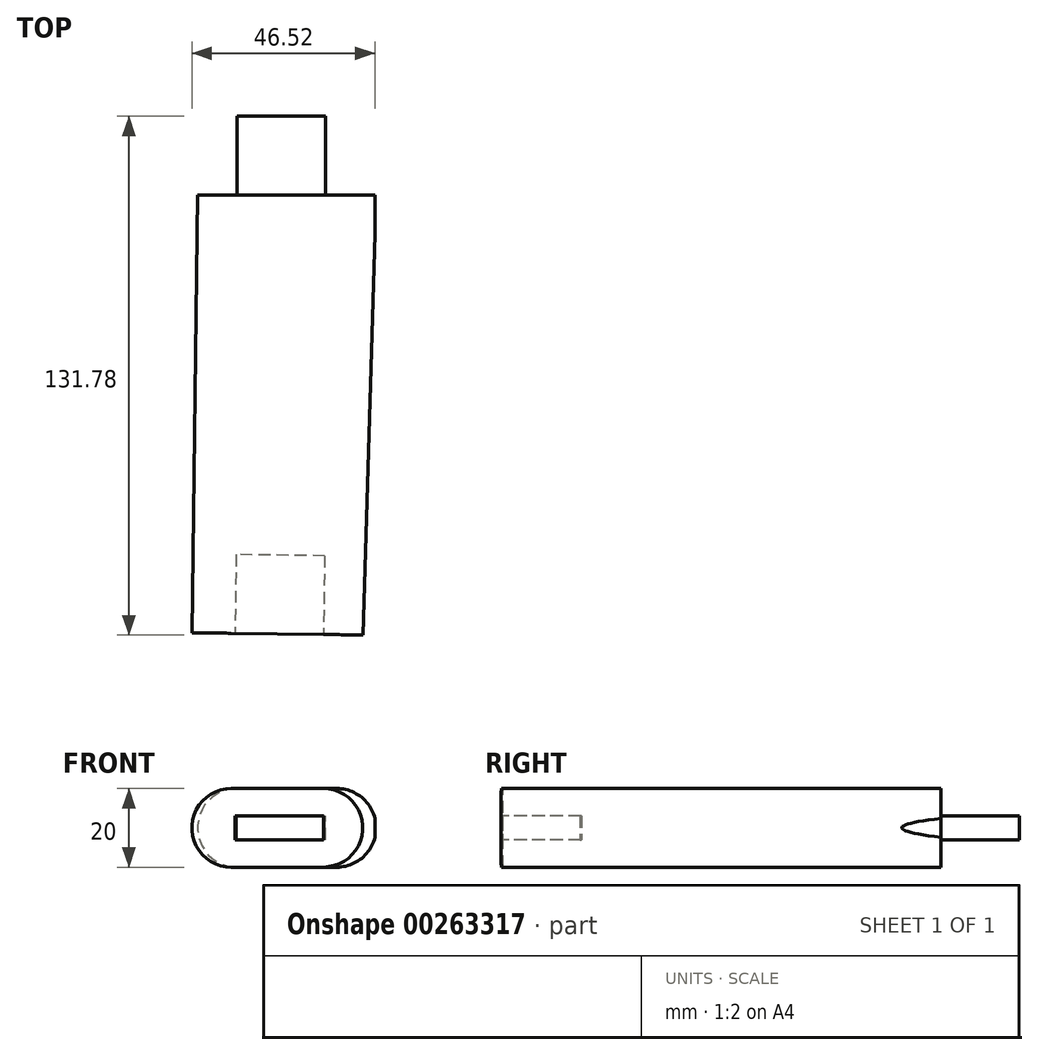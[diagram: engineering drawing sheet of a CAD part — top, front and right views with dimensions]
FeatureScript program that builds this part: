
annotation { "Feature Type Name" : "Feature", "Feature Type Description" : "" }
export const myFeature = defineFeature(function(context is Context, id is Id, definition is map)
    precondition{}
    {
        {
            var Q0;
            Q0=qCreatedBy(makeId("Top.planeOp"),FACE);
            var sketch = newSketch(context, id + "F0", { "sketchPlane" : qUnion([Q0])});
            skArc(sketch, "E0", {"start": v(-69.56, -48.3) * mm, "mid": v(-88.08, -45.25) * mm, "end": v(-106.8, -43.78) * mm});
            skArc(sketch, "E1", {"start": v(-106.8, -43.78) * mm, "mid": v(-96.39, -62.57) * mm, "end": v(-80.73, -77.27) * mm});
            skArc(sketch, "E2", {"start": v(-80.73, -77.27) * mm, "mid": v(-98.26, -84.7) * mm, "end": v(-114.23, -95.07) * mm});
            skArc(sketch, "E3", {"start": v(-114.23, -95.07) * mm, "mid": v(-98.6, -104.41) * mm, "end": v(-80.73, -107.98) * mm});
            skArc(sketch, "E4", {"start": v(-80.73, -107.98) * mm, "mid": v(-90.04, -123.58) * mm, "end": v(-94.69, -141.13) * mm});
            skArc(sketch, "E5", {"start": v(-94.69, -141.13) * mm, "mid": v(-78.8, -139.7) * mm, "end": v(-63.98, -133.8) * mm});
            skArc(sketch, "E6", {"start": v(-63.98, -133.8) * mm, "mid": v(40.14, -139.24) * mm, "end": v(30.94, -35.4) * mm});
            skArc(sketch, "E7", {"start": v(-31.41, -22.87) * mm, "mid": v(-53.17, -31.57) * mm, "end": v(-69.56, -48.3) * mm});
            skCircle(sketch, "E8", {"center": v(-12, -90) * mm, "radius": 35 * mm});
            skLineSegment(sketch, "E9", {"start": v(-12, -90) * mm, "end": v(-12, 0) * mm});
            skLineSegment(sketch, "E10", {"start": v(-12, 0) * mm, "end": v(0, 0) * mm});
            skLineSegment(sketch, "E11", {"start": v(-31.41, -22.87) * mm, "end": v(-12, 0) * mm});
            skLineSegment(sketch, "E12", {"start": v(-31.41, -22.87) * mm, "end": v(0, 0) * mm});
            skArc(sketch, "E13", {"start": v(30.94, -35.4) * mm, "mid": v(57.65, 8.29) * mm, "end": v(64.82, 58.99) * mm});
            skLineSegment(sketch, "E14", {"start": v(64.82, 42.9) * mm, "end": v(70.1, 125.75) * mm});
            skLineSegment(sketch, "E15", {"start": v(70.1, 125.75) * mm, "end": v(73.47, 146.99) * mm});
            skLineSegment(sketch, "E16", {"start": v(73.47, 146.99) * mm, "end": v(91.25, 150.97) * mm});
            skArc(sketch, "E17", {"start": v(93.55, 168.05) * mm, "mid": v(98.13, 170.3) * mm, "end": v(101.04, 174.5) * mm});
            skArc(sketch, "E18", {"start": v(101.04, 174.5) * mm, "mid": v(98.19, 178.86) * mm, "end": v(93.55, 181.22) * mm});
            skArc(sketch, "E19", {"start": v(91.25, 150.97) * mm, "mid": v(97.19, 153.5) * mm, "end": v(101.85, 157.96) * mm});
            skArc(sketch, "E20", {"start": v(101.85, 157.96) * mm, "mid": v(99.5, 164.5) * mm, "end": v(93.55, 168.05) * mm});
            skArc(sketch, "E21", {"start": v(93.55, 181.22) * mm, "mid": v(100.45, 185.24) * mm, "end": v(104.38, 192.2) * mm});
            skArc(sketch, "E22", {"start": v(16.27, 5.35) * mm, "mid": v(27.94, 20.47) * mm, "end": v(35.96, 37.8) * mm});
            skLineSegment(sketch, "E23", {"start": v(16.27, 5.35) * mm, "end": v(12.02, 0.97) * mm});
            skLineSegment(sketch, "E24", {"start": v(12.02, 54.47) * mm, "end": v(16.98, 220.58) * mm});
            skLineSegment(sketch, "E25", {"start": v(16.98, 220.58) * mm, "end": v(16.98, 230.48) * mm});
            skArc(sketch, "E26", {"start": v(20.74, 234.78) * mm, "mid": v(18.05, 233.34) * mm, "end": v(16.98, 230.48) * mm});
            skLineSegment(sketch, "E27", {"start": v(20.74, 234.78) * mm, "end": v(55.67, 234.78) * mm});
            skArc(sketch, "E28", {"start": v(55.67, 234.78) * mm, "mid": v(75.45, 242.82) * mm, "end": v(84, 262.38) * mm});
            skArc(sketch, "E29", {"start": v(84, 262.38) * mm, "mid": v(83.8, 275) * mm, "end": v(79.59, 286.9) * mm});
            skArc(sketch, "E30", {"start": v(79.59, 286.9) * mm, "mid": v(90.12, 305.47) * mm, "end": v(96.46, 325.87) * mm});
            skArc(sketch, "E31", {"start": v(96.46, 325.87) * mm, "mid": v(80.34, 314.22) * mm, "end": v(65.52, 300.95) * mm});
            skArc(sketch, "E32", {"start": v(65.52, 300.95) * mm, "mid": v(66.02, 314.82) * mm, "end": v(65.52, 328.68) * mm});
            skArc(sketch, "E33", {"start": v(41.86, 304.54) * mm, "mid": v(40.03, 315.53) * mm, "end": v(35.9, 325.87) * mm});
            skArc(sketch, "E34", {"start": v(35.9, 325.87) * mm, "mid": v(29.68, 316.4) * mm, "end": v(23.68, 306.81) * mm});
            skArc(sketch, "E35", {"start": v(23.68, 306.81) * mm, "mid": v(-21.12, 284.92) * mm, "end": v(-28, 235.53) * mm});
            skLineSegment(sketch, "E36", {"start": v(-31.41, -22.87) * mm, "end": v(-28, 235.53) * mm});
            skLineSegment(sketch, "E37", {"start": v(0, 0) * mm, "end": v(0, 302.13) * mm});
            skLineSegment(sketch, "E38", {"start": v(12.02, 0.97) * mm, "end": v(-31.41, -22.87) * mm});
            skLineSegment(sketch, "E39", {"start": v(0, 0) * mm, "end": v(12.02, 0.97) * mm});
            skLineSegment(sketch, "E40", {"start": v(12.02, 0.97) * mm, "end": v(30.94, -35.4) * mm});
            skLineSegment(sketch, "E41", {"start": v(64.82, 58.99) * mm, "end": v(46.6, 104.17) * mm});
            skLineSegment(sketch, "E42", {"start": v(12.02, 0.97) * mm, "end": v(12.02, 54.47) * mm});
            skLineSegment(sketch, "E43", {"start": v(-29.54, 119.27) * mm, "end": v(13.94, 118.7) * mm});
            skLineSegment(sketch, "E44", {"start": v(35.96, 37.8) * mm, "end": v(38.97, 138.47) * mm});
            skArc(sketch, "E45", {"start": v(104.38, 192.2) * mm, "mid": v(74.78, 206.52) * mm, "end": v(46.71, 189.39) * mm});
            skArc(sketch, "E46", {"start": v(46.71, 189.39) * mm, "mid": v(41.3, 164.16) * mm, "end": v(38.97, 138.47) * mm});
            skLineSegment(sketch, "E47", {"start": v(104.38, 192.2) * mm, "end": v(93.55, 181.22) * mm});
            skLineSegment(sketch, "E48", {"start": v(93.55, 168.05) * mm, "end": v(101.85, 157.96) * mm});
            skLineSegment(sketch, "E49", {"start": v(93.55, 181.22) * mm, "end": v(101.04, 174.5) * mm});
            skLineSegment(sketch, "E50", {"start": v(93.55, 168.05) * mm, "end": v(101.04, 174.5) * mm});
            skLineSegment(sketch, "E51", {"start": v(41.86, 304.54) * mm, "end": v(65.52, 328.68) * mm});
            skLineSegment(sketch, "E52", {"start": v(16.98, 230.48) * mm, "end": v(-28.07, 230.48) * mm});
            skLineSegment(sketch, "E53", {"start": v(12.02, 0.97) * mm, "end": v(-31.1, 0.49) * mm});
            skPoint(sketch, "E53.endSnap0", {"position": v(6.01, 0.49) * mm});
            skLineSegment(sketch, "E54", {"start": v(12.02, 0.97) * mm, "end": v(43.15, -20.17) * mm});
            skSolve(sketch);
        }
        {
            var Q0;
            {var subQ0=sQuery(id+"F0.wireOp",EDGE,"E38");var subQ1=sQuery(id+"F0.wireOp",EDGE,"E9");var subQ2=makeQuery(id+"F0.imprint","INTERSECT",VERTEX,{"derivedFrom":[subQ1,subQ0]});Q0=makeQuery(id+"F0.imprint","IMPRINT",FACE,{"disambiguationData":[TD([[makeQuery(id+"F0.imprint","IMPRINT",EDGE,{"disambiguationData":[TD([[subQ2,-1.0]])],"derivedFrom":subQ1}),1.0]])]});}
            var Q1;
            {var subQ0=sQuery(id+"F0.wireOp",EDGE,"E11");Q1=makeQuery(id+"F0.imprint","IMPRINT",FACE,{"disambiguationData":[TD([[makeQuery(id+"F0.imprint","IMPRINT",EDGE,{"derivedFrom":subQ0}),-1.0]])]});}
            var Q2;
            {var subQ0=sQuery(id+"F0.wireOp",EDGE,"E39");Q2=makeQuery(id+"F0.imprint","IMPRINT",FACE,{"disambiguationData":[TD([[makeQuery(id+"F0.imprint","IMPRINT",EDGE,{"derivedFrom":subQ0}),1.0]])]});}
            var Q3;
            Q3=makeQuery(id+"F0.imprint","IMPRINT",FACE,{"disambiguationData":[TD([[makeQuery(id+"F0.imprint","IMPRINT",EDGE,{"derivedFrom":sQuery(id+"F0.wireOp",EDGE,"E0")}),1.0]])]});
            var Q4;
            {var subQ5=sQuery(id+"F0.wireOp",EDGE,"E39");Q4=makeQuery(id+"F0.imprint","IMPRINT",FACE,{"disambiguationData":[TD([[makeQuery(id+"F0.imprint","IMPRINT",EDGE,{"derivedFrom":subQ5}),-1.0]])]});}
            var Q5;
            {var subQ2=sQuery(id+"F0.wireOp",EDGE,"E10");Q5=makeQuery(id+"F0.imprint","IMPRINT",FACE,{"disambiguationData":[TD([[makeQuery(id+"F0.imprint","IMPRINT",EDGE,{"derivedFrom":subQ2}),1.0]])]});}
            var Q6;
            {var subQ0=sQuery(id+"F0.wireOp",EDGE,"E10");Q6=makeQuery(id+"F0.imprint","IMPRINT",FACE,{"disambiguationData":[TD([[makeQuery(id+"F0.imprint","IMPRINT",EDGE,{"derivedFrom":subQ0}),-1.0]])]});}
            var Q7;
            {var subQ0=sQuery(id+"F0.wireOp",EDGE,"E40");Q7=makeQuery(id+"F0.imprint","IMPRINT",FACE,{"disambiguationData":[TD([[makeQuery(id+"F0.imprint","IMPRINT",EDGE,{"derivedFrom":subQ0}),1.0]])]});}
            extrude(context, id + "F1", {"entities" : qUnion([Q0, Q1, Q2, Q3, Q4, Q5, Q6, Q7]), "depth" : 20 * mm});
        }
        {
            var Q0;
            {var subQ1=sQuery(id+"F0.wireOp",EDGE,"E14");Q0=makeQuery(id+"F0.imprint","IMPRINT",FACE,{"disambiguationData":[TD([[makeQuery(id+"F0.imprint","IMPRINT",EDGE,{"derivedFrom":subQ1}),1.0]])]});}
            extrude(context, id + "F2", {"entities" : qUnion([Q0]), "depth" : 20 * mm});
        }
        {
            var Q0;
            {var subQ0=sQuery(id+"F0.wireOp",EDGE,"E43");var subQ1=sQuery(id+"F0.wireOp",EDGE,"E36");var subQ2=makeQuery(id+"F0.imprint","INTERSECT",VERTEX,{"derivedFrom":[subQ1,subQ0]});Q0=makeQuery(id+"F0.imprint","IMPRINT",FACE,{"disambiguationData":[TD([[makeQuery(id+"F0.imprint","IMPRINT",EDGE,{"disambiguationData":[TD([[subQ2,1.0]])],"derivedFrom":subQ1}),-1.0]])]});}
            var Q1;
            {var subQ5=sQuery(id+"F0.wireOp",EDGE,"E42");Q1=makeQuery(id+"F0.imprint","IMPRINT",FACE,{"disambiguationData":[TD([[makeQuery(id+"F0.imprint","IMPRINT",EDGE,{"derivedFrom":subQ5}),1.0]])]});}
            extrude(context, id + "F3", {"entities" : qUnion([Q0, Q1]), "depth" : 20 * mm});
        }
        {
            var Q0;
            {var subQ0=sQuery(id+"F0.wireOp",EDGE,"E36");var subQ1=sQuery(id+"F0.wireOp",EDGE,"E35");var subQ2=makeQuery(id+"F0.imprint","INTERSECT",VERTEX,{"derivedFrom":[subQ1,subQ0]});Q0=makeQuery(id+"F0.imprint","IMPRINT",FACE,{"disambiguationData":[TD([[makeQuery(id+"F0.imprint","IMPRINT",EDGE,{"disambiguationData":[TD([[subQ2,1.0]])],"derivedFrom":subQ1}),1.0]])]});}
            var Q1;
            {var subQ4=sQuery(id+"F0.wireOp",EDGE,"E26");Q1=makeQuery(id+"F0.imprint","IMPRINT",FACE,{"disambiguationData":[TD([[makeQuery(id+"F0.imprint","IMPRINT",EDGE,{"derivedFrom":subQ4}),-1.0]])]});}
            extrude(context, id + "F4", {"entities" : qUnion([Q0, Q1]), "depth" : 20 * mm});
        }
        {
            var Q0;
            {var subQ0=sQuery(id+"F0.wireOp",EDGE,"E43");var subQ1=sQuery(id+"F0.wireOp",EDGE,"E36");var subQ2=makeQuery(id+"F0.imprint","INTERSECT",VERTEX,{"derivedFrom":[subQ1,subQ0]});Q0=makeQuery(id+"F0.imprint","IMPRINT",FACE,{"disambiguationData":[TD([[makeQuery(id+"F0.imprint","IMPRINT",EDGE,{"disambiguationData":[TD([[subQ2,-1.0]])],"derivedFrom":subQ1}),-1.0]])]});}
            var Q1;
            {var subQ7=sQuery(id+"F0.wireOp",EDGE,"E25");Q1=makeQuery(id+"F0.imprint","IMPRINT",FACE,{"disambiguationData":[TD([[makeQuery(id+"F0.imprint","IMPRINT",EDGE,{"derivedFrom":subQ7}),1.0]])]});}
            extrude(context, id + "F5", {"entities" : qUnion([Q0, Q1]), "depth" : 20 * mm});
        }
        {
            var Q0;
            Q0=makeQuery(id+"F1.opExtrude","CAP_EDGE",EDGE,{"disambiguationData":[OSD([sQuery(id+"F0.wireOp",EDGE,"E36")])],"isStart":false});
            var Q1;
            Q1=makeQuery(id+"F1.opExtrude","CAP_EDGE",EDGE,{"disambiguationData":[OSD([sQuery(id+"F0.wireOp",EDGE,"E24")])],"isStart":false});
            var Q2;
            Q2=makeQuery(id+"F1.opExtrude","CAP_EDGE",EDGE,{"disambiguationData":[OSD([sQuery(id+"F0.wireOp",EDGE,"E42")])],"isStart":false});
            var Q3;
            Q3=makeQuery(id+"F1.opExtrude","CAP_EDGE",EDGE,{"disambiguationData":[OSD([sQuery(id+"F0.wireOp",EDGE,"E25")])],"isStart":false});
            var Q4;
            Q4=makeQuery(id+"F1.opExtrude","CAP_EDGE",EDGE,{"disambiguationData":[OSD([sQuery(id+"F0.wireOp",EDGE,"E35")])],"isStart":false});
            var Q5;
            Q5=makeQuery(id+"F1.opExtrude","CAP_EDGE",EDGE,{"disambiguationData":[OSD([sQuery(id+"F0.wireOp",EDGE,"E26")])],"isStart":false});
            var Q6;
            Q6=makeQuery(id+"F1.opExtrude","CAP_EDGE",EDGE,{"disambiguationData":[OSD([sQuery(id+"F0.wireOp",EDGE,"E42")])],"isStart":true});
            var Q7;
            Q7=makeQuery(id+"F1.opExtrude","CAP_EDGE",EDGE,{"disambiguationData":[OSD([sQuery(id+"F0.wireOp",EDGE,"E25")])],"isStart":true});
            var Q8;
            Q8=makeQuery(id+"F1.opExtrude","CAP_EDGE",EDGE,{"disambiguationData":[OSD([sQuery(id+"F0.wireOp",EDGE,"E36")])],"isStart":true});
            var Q9;
            Q9=makeQuery(id+"F1.opExtrude","CAP_EDGE",EDGE,{"disambiguationData":[OSD([sQuery(id+"F0.wireOp",EDGE,"E35")])],"isStart":true});
            var Q10;
            Q10=makeQuery(id+"F1.opExtrude","CAP_EDGE",EDGE,{"disambiguationData":[OSD([sQuery(id+"F0.wireOp",EDGE,"E26")])],"isStart":true});
            var Q11;
            Q11=makeQuery(id+"F1.opExtrude","CAP_EDGE",EDGE,{"disambiguationData":[OSD([sQuery(id+"F0.wireOp",EDGE,"E22")])],"isStart":false});
            var Q12;
            Q12=makeQuery(id+"F1.opExtrude","CAP_EDGE",EDGE,{"disambiguationData":[OSD([sQuery(id+"F0.wireOp",EDGE,"E23")])],"isStart":false});
            var Q13;
            Q13=makeQuery(id+"F1.opExtrude","CAP_EDGE",EDGE,{"disambiguationData":[OSD([sQuery(id+"F0.wireOp",EDGE,"E44")])],"isStart":false});
            var Q14;
            Q14=makeQuery(id+"F1.opExtrude","CAP_EDGE",EDGE,{"disambiguationData":[OSD([sQuery(id+"F0.wireOp",EDGE,"E45")])],"isStart":false});
            var Q15;
            Q15=makeQuery(id+"F1.opExtrude","CAP_EDGE",EDGE,{"disambiguationData":[OSD([sQuery(id+"F0.wireOp",EDGE,"E22")])],"isStart":true});
            var Q16;
            Q16=makeQuery(id+"F1.opExtrude","CAP_EDGE",EDGE,{"disambiguationData":[OSD([sQuery(id+"F0.wireOp",EDGE,"E44")])],"isStart":true});
            var Q17;
            Q17=makeQuery(id+"F1.opExtrude","CAP_EDGE",EDGE,{"disambiguationData":[OSD([sQuery(id+"F0.wireOp",EDGE,"E45")])],"isStart":true});
            var Q18;
            Q18=makeQuery(id+"F1.opExtrude","CAP_EDGE",EDGE,{"disambiguationData":[OSD([sQuery(id+"F0.wireOp",EDGE,"E13")])],"isStart":false});
            var Q19;
            Q19=makeQuery(id+"F1.opExtrude","CAP_EDGE",EDGE,{"disambiguationData":[OSD([sQuery(id+"F0.wireOp",EDGE,"E14")])],"isStart":false});
            var Q20;
            Q20=makeQuery(id+"F1.opExtrude","CAP_EDGE",EDGE,{"disambiguationData":[OSD([sQuery(id+"F0.wireOp",EDGE,"E15")])],"isStart":false});
            var Q21;
            Q21=makeQuery(id+"F1.opExtrude","CAP_EDGE",EDGE,{"disambiguationData":[OSD([sQuery(id+"F0.wireOp",EDGE,"E16")])],"isStart":false});
            var Q22;
            Q22=makeQuery(id+"F1.opExtrude","CAP_EDGE",EDGE,{"disambiguationData":[OSD([sQuery(id+"F0.wireOp",EDGE,"E16")])],"isStart":true});
            var Q23;
            Q23=makeQuery(id+"F1.opExtrude","CAP_EDGE",EDGE,{"disambiguationData":[OSD([sQuery(id+"F0.wireOp",EDGE,"E15")])],"isStart":true});
            var Q24;
            Q24=makeQuery(id+"F1.opExtrude","CAP_EDGE",EDGE,{"disambiguationData":[OSD([sQuery(id+"F0.wireOp",EDGE,"E14")])],"isStart":true});
            var Q25;
            Q25=makeQuery(id+"F1.opExtrude","CAP_EDGE",EDGE,{"disambiguationData":[OSD([sQuery(id+"F0.wireOp",EDGE,"E13")])],"isStart":true});
            var Q26;
            Q26=makeQuery(id+"F1.opExtrude","CAP_EDGE",EDGE,{"disambiguationData":[OSD([sQuery(id+"F0.wireOp",EDGE,"E6")])],"isStart":false});
            var Q27;
            Q27=makeQuery(id+"F1.opExtrude","CAP_EDGE",EDGE,{"disambiguationData":[OSD([sQuery(id+"F0.wireOp",EDGE,"E8")])],"isStart":false});
            var Q28;
            Q28=makeQuery(id+"F1.opExtrude","CAP_EDGE",EDGE,{"disambiguationData":[OSD([sQuery(id+"F0.wireOp",EDGE,"E7")])],"isStart":false});
            var Q29;
            Q29=makeQuery(id+"F1.opExtrude","CAP_EDGE",EDGE,{"disambiguationData":[OSD([sQuery(id+"F0.wireOp",EDGE,"E8")])],"isStart":true});
            var Q30;
            Q30=makeQuery(id+"F1.opExtrude","CAP_EDGE",EDGE,{"disambiguationData":[OSD([sQuery(id+"F0.wireOp",EDGE,"E7")])],"isStart":true});
            var Q31;
            Q31=makeQuery(id+"F1.opExtrude","CAP_EDGE",EDGE,{"disambiguationData":[OSD([sQuery(id+"F0.wireOp",EDGE,"E6")])],"isStart":true});
            fillet(context, id + "F6", {"entities" : qUnion([Q0, Q1, Q2, Q3, Q4, Q5, Q6, Q7, Q8, Q9, Q10, Q11, Q12, Q13, Q14, Q15, Q16, Q17, Q18, Q19, Q20, Q21, Q22, Q23, Q24, Q25, Q26, Q27, Q28, Q29, Q30, Q31]), "radius" : 10 * mm, "tangentPropagation" : true, "allowEdgeOverflow" : false});
        }
        {
            var Q0;
            Q0=makeQuery(id+"F1.opExtrude","CAP_EDGE",EDGE,{"disambiguationData":[OSD([sQuery(id+"F0.wireOp",EDGE,"E0")])],"isStart":false});
            var Q1;
            Q1=makeQuery(id+"F1.opExtrude","CAP_EDGE",EDGE,{"disambiguationData":[OSD([sQuery(id+"F0.wireOp",EDGE,"E1")])],"isStart":false});
            var Q2;
            Q2=makeQuery(id+"F1.opExtrude","CAP_EDGE",EDGE,{"disambiguationData":[OSD([sQuery(id+"F0.wireOp",EDGE,"E5")])],"isStart":false});
            var Q3;
            Q3=makeQuery(id+"F1.opExtrude","CAP_EDGE",EDGE,{"disambiguationData":[OSD([sQuery(id+"F0.wireOp",EDGE,"E4")])],"isStart":false});
            var Q4;
            Q4=makeQuery(id+"F1.opExtrude","CAP_EDGE",EDGE,{"disambiguationData":[OSD([sQuery(id+"F0.wireOp",EDGE,"E0")])],"isStart":true});
            var Q5;
            Q5=makeQuery(id+"F1.opExtrude","CAP_EDGE",EDGE,{"disambiguationData":[OSD([sQuery(id+"F0.wireOp",EDGE,"E1")])],"isStart":true});
            var Q6;
            Q6=makeQuery(id+"F1.opExtrude","CAP_EDGE",EDGE,{"disambiguationData":[OSD([sQuery(id+"F0.wireOp",EDGE,"E4")])],"isStart":true});
            var Q7;
            Q7=makeQuery(id+"F1.opExtrude","CAP_EDGE",EDGE,{"disambiguationData":[OSD([sQuery(id+"F0.wireOp",EDGE,"E5")])],"isStart":true});
            fillet(context, id + "F7", {"entities" : qUnion([Q0, Q1, Q2, Q3, Q4, Q5, Q6, Q7]), "radius" : 9.5 * mm, "tangentPropagation" : true, "rho" : 0.5, "crossSection" : FilletCrossSection.CONIC, "allowEdgeOverflow" : false});
        }
        {
            var Q0;
            Q0=makeQuery(id+"F1.opExtrude","CAP_EDGE",EDGE,{"disambiguationData":[OSD([sQuery(id+"F0.wireOp",EDGE,"E3")])],"isStart":true});
            var Q1;
            Q1=makeQuery(id+"F1.opExtrude","CAP_EDGE",EDGE,{"disambiguationData":[OSD([sQuery(id+"F0.wireOp",EDGE,"E2")])],"isStart":true});
            var Q2;
            Q2=makeQuery(id+"F1.opExtrude","CAP_EDGE",EDGE,{"disambiguationData":[OSD([sQuery(id+"F0.wireOp",EDGE,"E2")])],"isStart":false});
            var Q3;
            Q3=makeQuery(id+"F1.opExtrude","CAP_EDGE",EDGE,{"disambiguationData":[OSD([sQuery(id+"F0.wireOp",EDGE,"E3")])],"isStart":false});
            fillet(context, id + "F8", {"entities" : qUnion([Q0, Q1, Q2, Q3]), "radius" : 3 * mm, "tangentPropagation" : true, "allowEdgeOverflow" : false});
        }
        {
            var Q0;
            Q0=makeQuery(id+"F2.opExtrude","CAP_EDGE",EDGE,{"disambiguationData":[OSD([sQuery(id+"F0.wireOp",EDGE,"E14")])],"isStart":false});
            var Q1;
            Q1=makeQuery(id+"F2.opExtrude","CAP_EDGE",EDGE,{"disambiguationData":[OSD([sQuery(id+"F0.wireOp",EDGE,"E15")])],"isStart":false});
            var Q2;
            Q2=makeQuery(id+"F2.opExtrude","CAP_EDGE",EDGE,{"disambiguationData":[OSD([sQuery(id+"F0.wireOp",EDGE,"E14")])],"isStart":true});
            var Q3;
            Q3=makeQuery(id+"F2.opExtrude","CAP_EDGE",EDGE,{"disambiguationData":[OSD([sQuery(id+"F0.wireOp",EDGE,"E15")])],"isStart":true});
            var Q4;
            Q4=makeQuery(id+"F2.opExtrude","CAP_EDGE",EDGE,{"disambiguationData":[OSD([sQuery(id+"F0.wireOp",EDGE,"E16")])],"isStart":true});
            var Q5;
            Q5=makeQuery(id+"F2.opExtrude","CAP_EDGE",EDGE,{"disambiguationData":[OSD([sQuery(id+"F0.wireOp",EDGE,"E16")])],"isStart":false});
            var Q6;
            Q6=makeQuery(id+"F2.opExtrude","CAP_EDGE",EDGE,{"disambiguationData":[OSD([sQuery(id+"F0.wireOp",EDGE,"E45")])],"isStart":true});
            var Q7;
            Q7=makeQuery(id+"F2.opExtrude","CAP_EDGE",EDGE,{"disambiguationData":[OSD([sQuery(id+"F0.wireOp",EDGE,"E45")])],"isStart":false});
            var Q8;
            Q8=makeQuery(id+"F2.opExtrude","CAP_EDGE",EDGE,{"disambiguationData":[OSD([sQuery(id+"F0.wireOp",EDGE,"E46")])],"isStart":false});
            var Q9;
            Q9=makeQuery(id+"F2.opExtrude","CAP_EDGE",EDGE,{"disambiguationData":[OSD([sQuery(id+"F0.wireOp",EDGE,"E44")])],"isStart":false});
            var Q10;
            Q10=makeQuery(id+"F2.opExtrude","CAP_EDGE",EDGE,{"disambiguationData":[OSD([sQuery(id+"F0.wireOp",EDGE,"E22")])],"isStart":false});
            var Q11;
            Q11=makeQuery(id+"F2.opExtrude","CAP_EDGE",EDGE,{"disambiguationData":[OSD([sQuery(id+"F0.wireOp",EDGE,"E23")])],"isStart":false});
            var Q12;
            Q12=makeQuery(id+"F2.opExtrude","CAP_EDGE",EDGE,{"disambiguationData":[OSD([sQuery(id+"F0.wireOp",EDGE,"E46")])],"isStart":true});
            var Q13;
            Q13=makeQuery(id+"F2.opExtrude","CAP_EDGE",EDGE,{"disambiguationData":[OSD([sQuery(id+"F0.wireOp",EDGE,"E23")])],"isStart":true});
            var Q14;
            Q14=makeQuery(id+"F2.opExtrude","CAP_EDGE",EDGE,{"disambiguationData":[OSD([sQuery(id+"F0.wireOp",EDGE,"E22")])],"isStart":true});
            var Q15;
            Q15=makeQuery(id+"F2.opExtrude","CAP_EDGE",EDGE,{"disambiguationData":[OSD([sQuery(id+"F0.wireOp",EDGE,"E44")])],"isStart":true});
            var Q16;
            Q16=makeQuery(id+"F3.opExtrude","CAP_EDGE",EDGE,{"disambiguationData":[OSD([sQuery(id+"F0.wireOp",EDGE,"E24")])],"isStart":false});
            var Q17;
            Q17=makeQuery(id+"F3.opExtrude","CAP_EDGE",EDGE,{"disambiguationData":[OSD([sQuery(id+"F0.wireOp",EDGE,"E42")])],"isStart":false});
            var Q18;
            Q18=makeQuery(id+"F3.opExtrude","CAP_EDGE",EDGE,{"disambiguationData":[OSD([sQuery(id+"F0.wireOp",EDGE,"E42")])],"isStart":true});
            var Q19;
            Q19=makeQuery(id+"F3.opExtrude","CAP_EDGE",EDGE,{"disambiguationData":[OSD([sQuery(id+"F0.wireOp",EDGE,"E24")])],"isStart":true});
            var Q20;
            Q20=makeQuery(id+"F3.opExtrude","CAP_EDGE",EDGE,{"disambiguationData":[OSD([sQuery(id+"F0.wireOp",EDGE,"E25")])],"isStart":true});
            var Q21;
            Q21=makeQuery(id+"F3.opExtrude","CAP_EDGE",EDGE,{"disambiguationData":[OSD([sQuery(id+"F0.wireOp",EDGE,"E36")])],"isStart":false});
            var Q22;
            Q22=makeQuery(id+"F3.opExtrude","CAP_EDGE",EDGE,{"disambiguationData":[OSD([sQuery(id+"F0.wireOp",EDGE,"E36")])],"isStart":true});
            var Q23;
            Q23=makeQuery(id+"F4.opExtrude","CAP_EDGE",EDGE,{"disambiguationData":[OSD([sQuery(id+"F0.wireOp",EDGE,"E36")])],"isStart":true});
            var Q24;
            Q24=makeQuery(id+"F4.opExtrude","CAP_EDGE",EDGE,{"disambiguationData":[OSD([sQuery(id+"F0.wireOp",EDGE,"E36")])],"isStart":false});
            var Q25;
            Q25=makeQuery(id+"F4.opExtrude","CAP_EDGE",EDGE,{"disambiguationData":[OSD([sQuery(id+"F0.wireOp",EDGE,"E35")])],"isStart":true});
            var Q26;
            Q26=makeQuery(id+"F4.opExtrude","CAP_EDGE",EDGE,{"disambiguationData":[OSD([sQuery(id+"F0.wireOp",EDGE,"E35")])],"isStart":false});
            var Q27;
            Q27=makeQuery(id+"F4.opExtrude","CAP_EDGE",EDGE,{"disambiguationData":[OSD([sQuery(id+"F0.wireOp",EDGE,"E27")])],"isStart":false});
            var Q28;
            Q28=makeQuery(id+"F4.opExtrude","CAP_EDGE",EDGE,{"disambiguationData":[OSD([sQuery(id+"F0.wireOp",EDGE,"E28")])],"isStart":false});
            var Q29;
            Q29=makeQuery(id+"F4.opExtrude","CAP_EDGE",EDGE,{"disambiguationData":[OSD([sQuery(id+"F0.wireOp",EDGE,"E29")])],"isStart":false});
            var Q30;
            Q30=makeQuery(id+"F4.opExtrude","CAP_EDGE",EDGE,{"disambiguationData":[OSD([sQuery(id+"F0.wireOp",EDGE,"E27")])],"isStart":true});
            var Q31;
            Q31=makeQuery(id+"F4.opExtrude","CAP_EDGE",EDGE,{"disambiguationData":[OSD([sQuery(id+"F0.wireOp",EDGE,"E28")])],"isStart":true});
            var Q32;
            Q32=makeQuery(id+"F4.opExtrude","CAP_EDGE",EDGE,{"disambiguationData":[OSD([sQuery(id+"F0.wireOp",EDGE,"E29")])],"isStart":true});
            var Q33;
            Q33=makeQuery(id+"F4.opExtrude","CAP_EDGE",EDGE,{"disambiguationData":[OSD([sQuery(id+"F0.wireOp",EDGE,"E26")])],"isStart":false});
            var Q34;
            Q34=makeQuery(id+"F4.opExtrude","CAP_EDGE",EDGE,{"disambiguationData":[OSD([sQuery(id+"F0.wireOp",EDGE,"E26")])],"isStart":true});
            var Q35;
            Q35=makeQuery(id+"F4.opExtrude","CAP_EDGE",EDGE,{"disambiguationData":[OSD([sQuery(id+"F0.wireOp",EDGE,"E30")])],"isStart":false});
            var Q36;
            Q36=makeQuery(id+"F4.opExtrude","CAP_EDGE",EDGE,{"disambiguationData":[OSD([sQuery(id+"F0.wireOp",EDGE,"E31")])],"isStart":false});
            var Q37;
            Q37=makeQuery(id+"F4.opExtrude","CAP_EDGE",EDGE,{"disambiguationData":[OSD([sQuery(id+"F0.wireOp",EDGE,"E30")])],"isStart":true});
            var Q38;
            Q38=makeQuery(id+"F4.opExtrude","CAP_EDGE",EDGE,{"disambiguationData":[OSD([sQuery(id+"F0.wireOp",EDGE,"E31")])],"isStart":true});
            var Q39;
            Q39=makeQuery(id+"F4.opExtrude","CAP_EDGE",EDGE,{"disambiguationData":[OSD([sQuery(id+"F0.wireOp",EDGE,"E33")])],"isStart":false});
            var Q40;
            Q40=makeQuery(id+"F4.opExtrude","CAP_EDGE",EDGE,{"disambiguationData":[OSD([sQuery(id+"F0.wireOp",EDGE,"E34")])],"isStart":false});
            var Q41;
            Q41=makeQuery(id+"F4.opExtrude","CAP_EDGE",EDGE,{"disambiguationData":[OSD([sQuery(id+"F0.wireOp",EDGE,"E34")])],"isStart":true});
            var Q42;
            Q42=makeQuery(id+"F4.opExtrude","CAP_EDGE",EDGE,{"disambiguationData":[OSD([sQuery(id+"F0.wireOp",EDGE,"E33")])],"isStart":true});
            var Q43;
            Q43=makeQuery(id+"F5.opExtrude","CAP_EDGE",EDGE,{"disambiguationData":[OSD([sQuery(id+"F0.wireOp",EDGE,"E36")])],"isStart":true});
            var Q44;
            Q44=makeQuery(id+"F5.opExtrude","CAP_EDGE",EDGE,{"disambiguationData":[OSD([sQuery(id+"F0.wireOp",EDGE,"E24")])],"isStart":true});
            var Q45;
            Q45=makeQuery(id+"F5.opExtrude","CAP_EDGE",EDGE,{"disambiguationData":[OSD([sQuery(id+"F0.wireOp",EDGE,"E36")])],"isStart":false});
            var Q46;
            Q46=makeQuery(id+"F5.opExtrude","CAP_EDGE",EDGE,{"disambiguationData":[OSD([sQuery(id+"F0.wireOp",EDGE,"E24")])],"isStart":false});
            fillet(context, id + "F9", {"entities" : qUnion([Q0, Q1, Q2, Q3, Q4, Q5, Q6, Q7, Q8, Q9, Q10, Q11, Q12, Q13, Q14, Q15, Q16, Q17, Q18, Q19, Q20, Q21, Q22, Q23, Q24, Q25, Q26, Q27, Q28, Q29, Q30, Q31, Q32, Q33, Q34, Q35, Q36, Q37, Q38, Q39, Q40, Q41, Q42, Q43, Q44, Q45, Q46]), "radius" : 10 * mm, "tangentPropagation" : true, "allowEdgeOverflow" : false});
        }
        {
            var Q0;
            Q0=makeQuery(id+"F4.opExtrude","CAP_EDGE",EDGE,{"disambiguationData":[OSD([sQuery(id+"F0.wireOp",EDGE,"E51")])],"isStart":false});
            var Q1;
            Q1=makeQuery(id+"F4.opExtrude","CAP_EDGE",EDGE,{"disambiguationData":[OSD([sQuery(id+"F0.wireOp",EDGE,"E32")])],"isStart":false});
            var Q2;
            Q2=makeQuery(id+"F4.opExtrude","CAP_EDGE",EDGE,{"disambiguationData":[OSD([sQuery(id+"F0.wireOp",EDGE,"E32")])],"isStart":true});
            var Q3;
            Q3=makeQuery(id+"F4.opExtrude","CAP_EDGE",EDGE,{"disambiguationData":[OSD([sQuery(id+"F0.wireOp",EDGE,"E51")])],"isStart":true});
            fillet(context, id + "F10", {"entities" : qUnion([Q0, Q1, Q2, Q3]), "radius" : 5 * mm, "tangentPropagation" : true, "allowEdgeOverflow" : false});
        }
        {
            var Q0;
            Q0=makeQuery(id+"F2.opExtrude","CAP_EDGE",EDGE,{"disambiguationData":[OSD([sQuery(id+"F0.wireOp",EDGE,"E50")])],"isStart":true});
            var Q1;
            Q1=makeQuery(id+"F2.opExtrude","CAP_EDGE",EDGE,{"disambiguationData":[OSD([sQuery(id+"F0.wireOp",EDGE,"E49")])],"isStart":true});
            var Q2;
            Q2=makeQuery(id+"F2.opExtrude","CAP_EDGE",EDGE,{"disambiguationData":[OSD([sQuery(id+"F0.wireOp",EDGE,"E49")])],"isStart":false});
            var Q3;
            Q3=makeQuery(id+"F2.opExtrude","CAP_EDGE",EDGE,{"disambiguationData":[OSD([sQuery(id+"F0.wireOp",EDGE,"E50")])],"isStart":false});
            var Q4;
            Q4=makeQuery(id+"F9.opFillet","BLEND_EDGE",EDGE,{"blendedFrom":[makeQuery(id+"F2.opExtrude","CAP_EDGE",EDGE,{"disambiguationData":[OSD([sQuery(id+"F0.wireOp",EDGE,"E45")])],"isStart":false}),makeQuery(id+"F2.opExtrude","SWEPT_FACE",FACE,{"disambiguationData":[OSD([sQuery(id+"F0.wireOp",EDGE,"E47")])]})],"blendedInto":[makeQuery(id+"F2.opExtrude","SWEPT_FACE",FACE,{"disambiguationData":[OSD([sQuery(id+"F0.wireOp",EDGE,"E47")])]})]});
            var Q5;
            Q5=makeQuery(id+"F9.opFillet","BLEND_EDGE",EDGE,{"blendedFrom":[makeQuery(id+"F2.opExtrude","CAP_EDGE",EDGE,{"disambiguationData":[OSD([sQuery(id+"F0.wireOp",EDGE,"E19")])],"isStart":false}),makeQuery(id+"F2.opExtrude","SWEPT_FACE",FACE,{"disambiguationData":[OSD([sQuery(id+"F0.wireOp",EDGE,"E48")])]})],"blendedInto":[makeQuery(id+"F2.opExtrude","SWEPT_FACE",FACE,{"disambiguationData":[OSD([sQuery(id+"F0.wireOp",EDGE,"E48")])]})]});
            fillet(context, id + "F11", {"entities" : qUnion([Q0, Q1, Q2, Q3, Q4, Q5]), "radius" : 5 * mm, "tangentPropagation" : true, "allowEdgeOverflow" : false});
        }
        {
            var Q0;
            Q0=makeQuery(id+"F6.opFillet","SPLIT",FACE,{"disambiguationData":[OD(0.0)],"derivedFrom":makeQuery(id+"F1.opExtrude","CAP_FACE",FACE,{"disambiguationData":[OSD([sQuery(id+"F0.wireOp",EDGE,"E0"),sQuery(id+"F0.wireOp",EDGE,"E1"),sQuery(id+"F0.wireOp",EDGE,"E2"),sQuery(id+"F0.wireOp",EDGE,"E3"),sQuery(id+"F0.wireOp",EDGE,"E4"),sQuery(id+"F0.wireOp",EDGE,"E5"),sQuery(id+"F0.wireOp",EDGE,"E6"),sQuery(id+"F0.wireOp",EDGE,"E7"),sQuery(id+"F0.wireOp",EDGE,"E8"),sQuery(id+"F0.wireOp",EDGE,"E13"),sQuery(id+"F0.wireOp",EDGE,"E14"),sQuery(id+"F0.wireOp",EDGE,"E15"),sQuery(id+"F0.wireOp",EDGE,"E16"),sQuery(id+"F0.wireOp",EDGE,"E19"),sQuery(id+"F0.wireOp",EDGE,"E22"),sQuery(id+"F0.wireOp",EDGE,"E23"),sQuery(id+"F0.wireOp",EDGE,"E24"),sQuery(id+"F0.wireOp",EDGE,"E25"),sQuery(id+"F0.wireOp",EDGE,"E26"),sQuery(id+"F0.wireOp",EDGE,"E27"),sQuery(id+"F0.wireOp",EDGE,"E28"),sQuery(id+"F0.wireOp",EDGE,"E29"),sQuery(id+"F0.wireOp",EDGE,"E30"),sQuery(id+"F0.wireOp",EDGE,"E31"),sQuery(id+"F0.wireOp",EDGE,"E32"),sQuery(id+"F0.wireOp",EDGE,"E33"),sQuery(id+"F0.wireOp",EDGE,"E34"),sQuery(id+"F0.wireOp",EDGE,"E35"),sQuery(id+"F0.wireOp",EDGE,"E36"),sQuery(id+"F0.wireOp",EDGE,"E42"),sQuery(id+"F0.wireOp",EDGE,"E44"),sQuery(id+"F0.wireOp",EDGE,"E45"),sQuery(id+"F0.wireOp",EDGE,"E46"),sQuery(id+"F0.wireOp",EDGE,"E47"),sQuery(id+"F0.wireOp",EDGE,"E48"),sQuery(id+"F0.wireOp",EDGE,"E49"),sQuery(id+"F0.wireOp",EDGE,"E50"),sQuery(id+"F0.wireOp",EDGE,"E51")])],"isStart":false})});
            var sketch = newSketch(context, id + "F12", { "sketchPlane" : qUnion([Q0])});
            skLineSegment(sketch, "E55", {"start": v(0, 0) * mm, "end": v(3.83, 289.97) * mm});
            skLineSegment(sketch, "E56", {"start": v(3.83, 289.97) * mm, "end": v(19.83, 289.76) * mm});
            skCircle(sketch, "E57", {"center": v(19.83, 289.76) * mm, "radius": 10 * mm});
            skSolve(sketch);
        }
        {
            var Q0;
            Q0=makeQuery(id+"F12.imprint","IMPRINT",FACE,{"disambiguationData":[TD([[makeQuery(id+"F12.imprint","IMPRINT",EDGE,{"derivedFrom":sQuery(id+"F12.wireOp",EDGE,"E57")}),1.0]])]});
            extrude(context, id + "F13", {"entities" : qUnion([Q0]), "operationType" : NewBodyOperationType.ADD, "depth" : 5 * mm, "hasSecondDirection" : true, "secondDirectionOppositeDirection" : true, "secondDirectionDepth" : 25 * mm});
        }
        {
            var Q0;
            Q0=makeQuery(id+"F13.opExtrude","CAP_EDGE",EDGE,{"disambiguationData":[OSD([sQuery(id+"F12.wireOp",EDGE,"E57")])],"isStart":false});
            chamfer(context, id + "F14", {"entities" : qUnion([Q0]), "chamferType" : ChamferType.OFFSET_ANGLE, "width" : 7 * mm, "oppositeDirection" : false, "angle" : 30 * degree, "tangentPropagation" : true});
        }
        {
            var Q0;
            Q0=makeQuery(id+"F13.opExtrude","CAP_EDGE",EDGE,{"disambiguationData":[OSD([sQuery(id+"F12.wireOp",EDGE,"E57")])],"isStart":true});
            chamfer(context, id + "F15", {"entities" : qUnion([Q0]), "chamferType" : ChamferType.OFFSET_ANGLE, "width" : 4 * mm, "oppositeDirection" : false, "angle" : 60 * degree, "tangentPropagation" : true});
        }
        {
            var Q0;
            Q0=makeQuery(id+"F1.opExtrude","SWEPT_BODY",BODY,{"disambiguationData":[OSD([sQuery(id+"F0.wireOp",EDGE,"E0"),sQuery(id+"F0.wireOp",EDGE,"E1"),sQuery(id+"F0.wireOp",EDGE,"E2"),sQuery(id+"F0.wireOp",EDGE,"E3"),sQuery(id+"F0.wireOp",EDGE,"E4"),sQuery(id+"F0.wireOp",EDGE,"E5"),sQuery(id+"F0.wireOp",EDGE,"E6"),sQuery(id+"F0.wireOp",EDGE,"E7"),sQuery(id+"F0.wireOp",EDGE,"E8"),sQuery(id+"F0.wireOp",EDGE,"E13"),sQuery(id+"F0.wireOp",EDGE,"E36"),sQuery(id+"F0.wireOp",EDGE,"E53"),sQuery(id+"F0.wireOp",EDGE,"E54")])]});
            var Q1;
            Q1=makeQuery(id+"F2.opExtrude","SWEPT_BODY",BODY,{"disambiguationData":[OSD([sQuery(id+"F0.wireOp",EDGE,"E13"),sQuery(id+"F0.wireOp",EDGE,"E14"),sQuery(id+"F0.wireOp",EDGE,"E15"),sQuery(id+"F0.wireOp",EDGE,"E16"),sQuery(id+"F0.wireOp",EDGE,"E19"),sQuery(id+"F0.wireOp",EDGE,"E22"),sQuery(id+"F0.wireOp",EDGE,"E23"),sQuery(id+"F0.wireOp",EDGE,"E44"),sQuery(id+"F0.wireOp",EDGE,"E45"),sQuery(id+"F0.wireOp",EDGE,"E46"),sQuery(id+"F0.wireOp",EDGE,"E47"),sQuery(id+"F0.wireOp",EDGE,"E48"),sQuery(id+"F0.wireOp",EDGE,"E49"),sQuery(id+"F0.wireOp",EDGE,"E50"),sQuery(id+"F0.wireOp",EDGE,"E54")])]});
            var Q2;
            Q2=makeQuery(id+"F4.opExtrude","SWEPT_BODY",BODY,{"disambiguationData":[OSD([sQuery(id+"F0.wireOp",EDGE,"E26"),sQuery(id+"F0.wireOp",EDGE,"E27"),sQuery(id+"F0.wireOp",EDGE,"E28"),sQuery(id+"F0.wireOp",EDGE,"E29"),sQuery(id+"F0.wireOp",EDGE,"E30"),sQuery(id+"F0.wireOp",EDGE,"E31"),sQuery(id+"F0.wireOp",EDGE,"E32"),sQuery(id+"F0.wireOp",EDGE,"E33"),sQuery(id+"F0.wireOp",EDGE,"E34"),sQuery(id+"F0.wireOp",EDGE,"E35"),sQuery(id+"F0.wireOp",EDGE,"E36"),sQuery(id+"F0.wireOp",EDGE,"E51"),sQuery(id+"F0.wireOp",EDGE,"E52")])]});
            deleteBodies(context, id + "F16", {"entities" : qUnion([Q0, Q1, Q2])});
        }
        {
            var Q0;
            Q0=makeQuery(id+"F3.opExtrude","SWEPT_FACE",FACE,{"disambiguationData":[OSD([sQuery(id+"F0.wireOp",EDGE,"E53")])]});
            var sketch = newSketch(context, id + "F17", { "sketchPlane" : qUnion([Q0])});
            skLineSegment(sketch, "E58", {"start": v(-31.1, 10) * mm, "end": v(-21.1, 10) * mm});
            skLineSegment(sketch, "E59", {"start": v(-21.1, 10) * mm, "end": v(-21.1, 13) * mm});
            skLineSegment(sketch, "E60.bottom", {"start": v(-21.1, 13) * mm, "end": v(1.4, 13) * mm});
            skLineSegment(sketch, "E60.top", {"start": v(-21.1, 7) * mm, "end": v(1.4, 7) * mm});
            skLineSegment(sketch, "E60.left", {"start": v(-21.1, 13) * mm, "end": v(-21.1, 7) * mm});
            skLineSegment(sketch, "E60.right", {"start": v(1.4, 13) * mm, "end": v(1.4, 7) * mm});
            skSolve(sketch);
        }
        {
            var Q0;
            Q0=qSketchRegion(id+"F17",true);
            extrude(context, id + "F18", {"entities" : qUnion([Q0]), "operationType" : NewBodyOperationType.ADD, "depth" : 20 * mm});
        }
        {
            var Q0;
            Q0=makeQuery(id+"F5.opExtrude","SWEPT_FACE",FACE,{"disambiguationData":[OSD([sQuery(id+"F0.wireOp",EDGE,"E52")])]});
            var sketch = newSketch(context, id + "F19", { "sketchPlane" : qUnion([Q0])});
            skLineSegment(sketch, "E61", {"start": v(18.07, 10) * mm, "end": v(18.07, 7) * mm});
            skLineSegment(sketch, "E62.bottom", {"start": v(18.07, 7) * mm, "end": v(-4.43, 7) * mm});
            skLineSegment(sketch, "E62.top", {"start": v(18.07, 13) * mm, "end": v(-4.43, 13) * mm});
            skLineSegment(sketch, "E62.left", {"start": v(18.07, 7) * mm, "end": v(18.07, 13) * mm});
            skLineSegment(sketch, "E62.right", {"start": v(-4.43, 7) * mm, "end": v(-4.43, 13) * mm});
            skLineSegment(sketch, "E63", {"start": v(28.07, 10) * mm, "end": v(28.07, 20) * mm});
            skLineSegment(sketch, "E64", {"start": v(28.07, 10) * mm, "end": v(28.07, 0) * mm});
            skLineSegment(sketch, "E65", {"start": v(2.06, 0) * mm, "end": v(2.06, 7) * mm});
            skLineSegment(sketch, "E66", {"start": v(18.07, 7) * mm, "end": v(2.06, 0) * mm});
            skSolve(sketch);
        }
        {
            var Q0;
            {var subQ4=sQuery(id+"F19.wireOp",EDGE,"E62.top");Q0=makeQuery(id+"F19.imprint","IMPRINT",FACE,{"disambiguationData":[TD([[makeQuery(id+"F19.imprint","IMPRINT",EDGE,{"derivedFrom":subQ4}),1.0]])]});}
            extrude(context, id + "F20", {"entities" : qUnion([Q0]), "operationType" : NewBodyOperationType.ADD, "depth" : 20 * mm});
        }
        {
            var Q0;
            Q0=makeQuery(id+"F3.opExtrude","SWEPT_BODY",BODY,{"disambiguationData":[OSD([sQuery(id+"F0.wireOp",EDGE,"E24"),sQuery(id+"F0.wireOp",EDGE,"E36"),sQuery(id+"F0.wireOp",EDGE,"E42"),sQuery(id+"F0.wireOp",EDGE,"E43"),sQuery(id+"F0.wireOp",EDGE,"E53")])]});
            deleteBodies(context, id + "F21", {"entities" : qUnion([Q0])});
        }
        {
            var Q0;
            Q0=makeQuery(id+"F5.opExtrude","SWEPT_FACE",FACE,{"disambiguationData":[OSD([sQuery(id+"F0.wireOp",EDGE,"E43")])]});
            var sketch = newSketch(context, id + "F22", { "sketchPlane" : qUnion([Q0])});
            skLineSegment(sketch, "E67", {"start": v(12.37, 10) * mm, "end": v(2.37, 10) * mm});
            skLineSegment(sketch, "E68", {"start": v(2.37, 10) * mm, "end": v(2.37, 13) * mm});
            skLineSegment(sketch, "E69.bottom", {"start": v(2.37, 13) * mm, "end": v(-20.13, 13) * mm});
            skLineSegment(sketch, "E69.top", {"start": v(2.37, 7) * mm, "end": v(-20.13, 7) * mm});
            skLineSegment(sketch, "E69.left", {"start": v(2.37, 13) * mm, "end": v(2.37, 7) * mm});
            skLineSegment(sketch, "E69.right", {"start": v(-20.13, 13) * mm, "end": v(-20.13, 7) * mm});
            skSolve(sketch);
        }
        {
            var Q0;
            Q0 = qSketchRegion(id + "F22", true);
            extrude(context, id + "F23", {"entities" : qUnion([Q0]), "operationType" : NewBodyOperationType.REMOVE, "oppositeDirection" : true, "depth" : 20 * mm});
        }
    });
